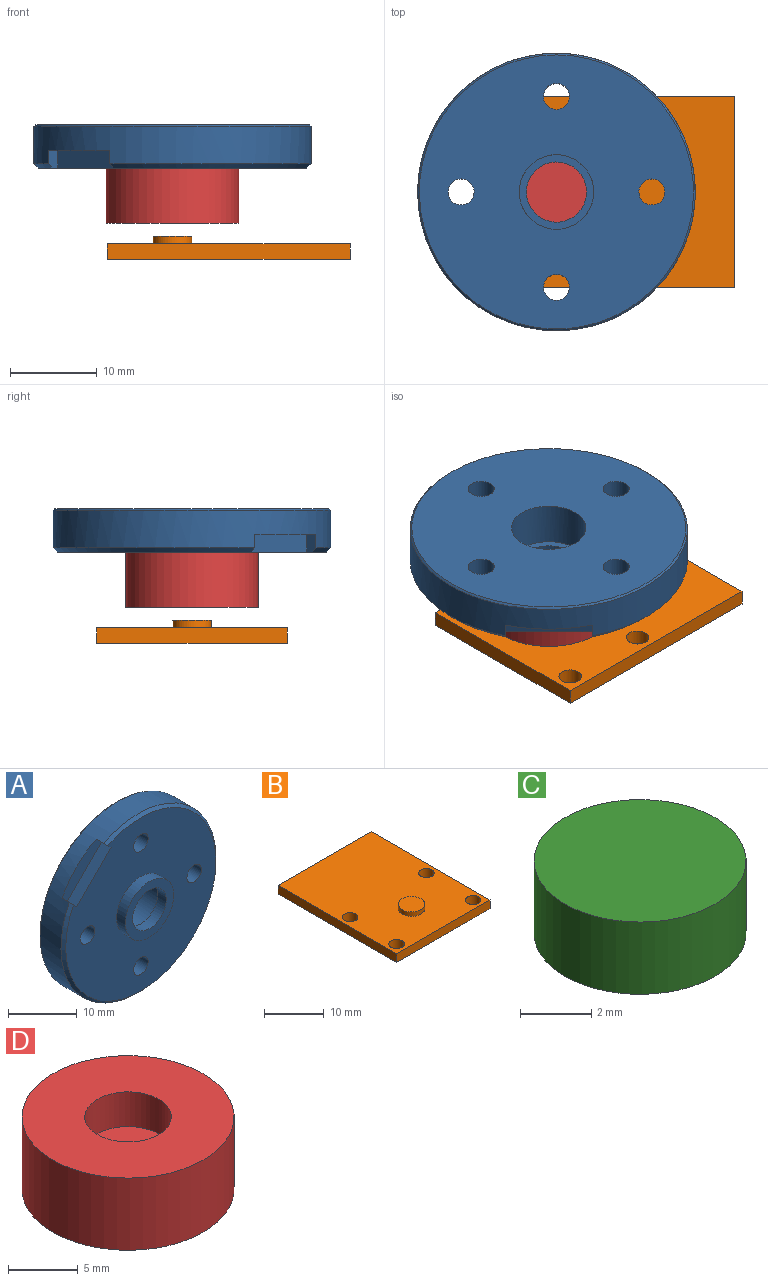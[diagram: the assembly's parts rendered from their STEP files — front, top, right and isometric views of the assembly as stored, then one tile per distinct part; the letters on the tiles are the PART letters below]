
ASSEMBLY  parts=4 mates=4
PART A: 18 faces, bbox 32x6.8x32 mm
  f0: cylinder r=16mm len=32mm, axis (0,1,0), area 417.1mm2, adj f4,f5,f10,f11,f12
  f1: plane 31x31mm, normal (0,-1,0), area 633.1mm2, adj f5,f6,f7,f8,f9,f11,f12,f13
  f2: plane 31.6x31.6mm, normal (0,1,0), area 697.9mm2, adj f3,f4,f6,f7,f8,f9
  f3: cylinder r=4.3mm len=8.6mm, axis (0,1,0), area 135.1mm2, adj f2,f14
  f4: cone r=16mm half-angle=45deg, axis (0,-1,0), area 28.3mm2, adj f0,f2
  f5: cone r=15.5mm half-angle=45deg, axis (0,1,0), area 62.8mm2, adj f0,f1,f11,f12
  f6: cylinder r=1.5mm len=5mm, axis (0,-1,0), area 47.1mm2, adj f1,f2
  f7: cylinder r=1.5mm len=5mm, axis (0,-1,0), area 47.1mm2, adj f1,f2
  f8: cylinder r=1.5mm len=5mm, axis (0,-1,0), area 47.1mm2, adj f1,f2
  f9: cylinder r=1.5mm len=5mm, axis (0,-1,0), area 47.1mm2, adj f1,f2
  f10: plane 8.12x8.12mm, normal (0,-1,0), area 20.3mm2, adj f0,f11,f12,f13
  f11: plane 2x1.06mm, normal (-0.71,0,-0.71), area 2.9mm2, adj f0,f1,f5,f10,f13
  f12: plane 2x1.06mm, normal (0.71,0,0.71), area 2.9mm2, adj f0,f1,f5,f10,f13
  f13: plane 7.06x7.06mm, normal (-0.71,0,0.71), area 20mm2, adj f1,f10,f11,f12
  f14: plane 8.6x8.6mm, normal (0,1,0), area 20.3mm2, adj f3,f16
  f15: cylinder r=4.99mm len=9.98mm, axis (0,1,0), area 55.8mm2, adj f1,f17
  f16: cylinder r=3.47mm len=6.93mm, axis (0,1,0), area 38.7mm2, adj f14,f17
  f17: plane 9.98x9.98mm, normal (0,-1,0), area 40.5mm2, adj f15,f16
PART B: 12 faces, bbox 22x28x2.7 mm
  f0: plane 28x1.78mm, normal (-1,0,0), area 49.8mm2, adj f1,f4,f8,f9
  f1: plane 22x1.78mm, normal (0,-1,0), area 39.1mm2, adj f0,f2,f8,f9
  f2: plane 28x1.78mm, normal (1,0,0), area 49.8mm2, adj f1,f4,f8,f9
  f3: cylinder r=1.3mm len=2.6mm, axis (0,0,-1), area 14.5mm2, adj f8,f9
  f4: plane 22x1.78mm, normal (0,1,0), area 39.1mm2, adj f0,f2,f8,f9
  f5: cylinder r=1.3mm len=2.6mm, axis (0,0,-1), area 14.5mm2, adj f8,f9
  f6: cylinder r=1.3mm len=2.6mm, axis (0,0,-1), area 14.5mm2, adj f8,f9
  f7: cylinder r=1.3mm len=2.6mm, axis (0,0,-1), area 14.5mm2, adj f8,f9
  f8: plane 28x22mm, normal (0,0,1), area 579.1mm2, adj f0,f1,f2,f3,f4,f5,f6,f7
  f9: plane 28x22mm, normal (0,0,-1), area 594.8mm2, adj f0,f1,f2,f3,f4,f5,f6,f7
  f10: cylinder r=2.23mm len=4.46mm, axis (0,0,-1), area 12.5mm2, adj f8,f11
  f11: plane 4.46x4.46mm, normal (0,0,1), area 15.6mm2, adj f10
PART C: 3 faces, bbox 6x6x2.5 mm
  f0: cylinder r=2.98mm len=5.97mm, axis (0,0,-1), area 46.7mm2, adj f1,f2
  f1: plane 5.97x5.97mm, normal (0,0,1), area 28mm2, adj f0
  f2: plane 5.97x5.97mm, normal (0,0,-1), area 28mm2, adj f0
PART D: 7 faces, bbox 15.2x15.2x6.4 mm
  f0: cylinder r=7.62mm len=15.24mm, axis (0,0,-1), area 304mm2, adj f1,f2
  f1: plane 15.24x15.24mm, normal (0,0,1), area 152mm2, adj f0,f5
  f2: plane 15.24x15.24mm, normal (0,0,-1), area 100.1mm2, adj f0,f3
  f3: cylinder r=5.12mm len=10.24mm, axis (0,0,-1), area 40.8mm2, adj f2,f4
  f4: plane 10.24x10.24mm, normal (0,0,-1), area 82.3mm2, adj f3
  f5: cylinder r=3.11mm len=6.22mm, axis (0,0,1), area 59.6mm2, adj f1,f6
  f6: plane 6.22x6.22mm, normal (0,0,1), area 30.4mm2, adj f5
PLACE A rot(axis=(1,0,0),90deg) t=(-11.11,8.45,5.47)mm
PLACE B rot(axis=(0,0,-1),90deg) t=(-11.11,8.45,-10.54)mm
PLACE C t=(-11.11,8.45,-5.82)mm
PLACE D rot(axis=(1,0,0),180deg) t=(-11.11,8.45,-0.03)mm
MATE cylindrical B.f10 <-> D.f0  axis (0,0,-1) through (-11.11,8.45,-8.32)mm
MATE slider D.f0 <-> C.f0  axis (0,0,-1) through (-11.11,8.45,-3.33)mm
MATE fastened B.f10 <-> D.f0  axis (0,0,1) through (-11.11,8.45,-7.88)mm
MATE slider D.f0 <-> A.f0  axis (0,0,1) through (-11.11,8.45,-1.3)mm
